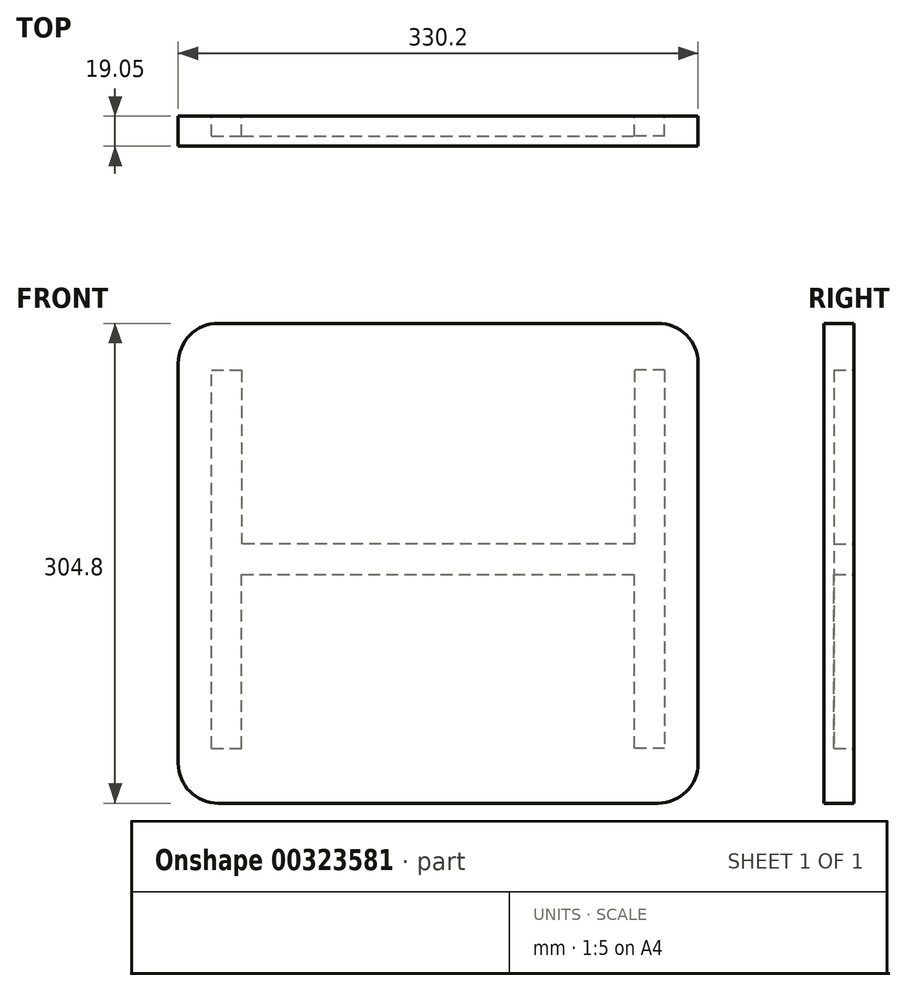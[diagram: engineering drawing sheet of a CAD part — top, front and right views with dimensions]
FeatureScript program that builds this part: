
annotation { "Feature Type Name" : "Feature", "Feature Type Description" : "" }
export const myFeature = defineFeature(function(context is Context, id is Id, definition is map)
    precondition{}
    {
        {
            var Q0;
            Q0=qCreatedBy(makeId("Front.planeOp"),FACE);
            var sketch = newSketch(context, id + "F0", { "sketchPlane" : qUnion([Q0])});
            skLineSegment(sketch, "E0", {"start": v(0, 163.43) * mm, "end": v(165.1, 163.43) * mm});
            skLineSegment(sketch, "E1.MirrorCS", {"start": v(0, 163.43) * mm, "end": v(-165.1, 163.43) * mm});
            skLineSegment(sketch, "E2", {"start": v(-165.1, 163.43) * mm, "end": v(-165.1, -141.37) * mm});
            skLineSegment(sketch, "E3", {"start": v(165.1, 163.43) * mm, "end": v(165.1, -141.37) * mm});
            skLineSegment(sketch, "E4", {"start": v(165.1, -141.37) * mm, "end": v(-165.1, -141.37) * mm});
            skSolve(sketch);
        }
        {
            var Q0;
            Q0 = qSketchRegion(id + "F0", true);
            extrude(context, id + "F1", {"entities" : qUnion([Q0]), "depth" : 19.05 * mm});
        }
        {
            var Q0;
            Q0=qCreatedBy(makeId("Front.planeOp"),FACE);
            var sketch = newSketch(context, id + "F2", { "sketchPlane" : qUnion([Q0])});
            skLineSegment(sketch, "E5", {"start": v(-166.8, 13.7) * mm, "end": v(0, 13.7) * mm, "construction": true});
            skLineSegment(sketch, "E6", {"start": v(0, -142.51) * mm, "end": v(0, 164.75) * mm, "construction": true});
            skLineSegment(sketch, "E7", {"start": v(0, 13.7) * mm, "end": v(165.2, 13.7) * mm, "construction": true});
            skLineSegment(sketch, "E8", {"start": v(143.88, 13.7) * mm, "end": v(143.88, 133.83) * mm});
            skLineSegment(sketch, "E9", {"start": v(143.88, 133.83) * mm, "end": v(124.83, 133.83) * mm});
            skLineSegment(sketch, "E10", {"start": v(124.83, 133.83) * mm, "end": v(124.83, 13.7) * mm});
            skLineSegment(sketch, "E11.MirrorCS", {"start": v(124.83, -106.45) * mm, "end": v(124.83, 13.7) * mm});
            skLineSegment(sketch, "E12.MirrorCS", {"start": v(143.88, 13.7) * mm, "end": v(143.88, -106.45) * mm});
            skLineSegment(sketch, "E13.MirrorCS", {"start": v(143.88, -106.45) * mm, "end": v(124.83, -106.45) * mm});
            skLineSegment(sketch, "E14.MirrorCS", {"start": v(-124.83, 133.83) * mm, "end": v(-124.83, 13.7) * mm});
            skLineSegment(sketch, "E15.MirrorCS", {"start": v(-143.88, 133.83) * mm, "end": v(-124.83, 133.83) * mm});
            skLineSegment(sketch, "E16.MirrorCS", {"start": v(-143.88, 13.7) * mm, "end": v(-143.88, 133.83) * mm});
            skLineSegment(sketch, "E17.MirrorCS", {"start": v(-143.88, 13.7) * mm, "end": v(-143.88, -106.45) * mm});
            skLineSegment(sketch, "E18.MirrorCS", {"start": v(-124.83, -106.45) * mm, "end": v(-124.83, 13.7) * mm});
            skLineSegment(sketch, "E19.MirrorCS", {"start": v(-143.88, -106.45) * mm, "end": v(-124.83, -106.45) * mm});
            skLineSegment(sketch, "E20", {"start": v(124.83, 133.83) * mm, "end": v(-124.83, 133.83) * mm, "construction": true});
            skLineSegment(sketch, "E21", {"start": v(110.9, 13.7) * mm, "end": v(110.9, 23.34) * mm, "construction": true});
            skLineSegment(sketch, "E22.MirrorCS", {"start": v(110.9, 13.7) * mm, "end": v(110.9, 4.04) * mm, "construction": true});
            skLineSegment(sketch, "E23", {"start": v(124.83, 23.34) * mm, "end": v(-124.83, 23.34) * mm});
            skLineSegment(sketch, "E24", {"start": v(-124.83, 23.34) * mm, "end": v(-124.83, 4.04) * mm});
            skLineSegment(sketch, "E25", {"start": v(-124.83, 4.04) * mm, "end": v(124.83, 4.04) * mm});
            skLineSegment(sketch, "E26", {"start": v(124.83, 4.04) * mm, "end": v(124.83, 23.34) * mm});
            skSolve(sketch);
        }
        {
            var Q0;
            Q0 = qSketchRegion(id + "F2", true);
            extrude(context, id + "F3", {"entities" : qUnion([Q0]), "operationType" : NewBodyOperationType.REMOVE, "depth" : 12.7 * mm});
        }
        {
            var Q0;
            Q0=makeQuery(id+"F1.opExtrude","SWEPT_EDGE",EDGE,{"disambiguationData":[OSD([sQuery(id+"F0.wireOp",EDGE,"E0"),sQuery(id+"F0.wireOp",EDGE,"E3")])]});
            fillet(context, id + "F4", {"entities" : qUnion([Q0]), "radius" : 25.4 * mm, "tangentPropagation" : true, "allowEdgeOverflow" : false});
        }
        {
            var Q0;
            Q0=makeQuery(id+"F1.opExtrude","SWEPT_EDGE",EDGE,{"disambiguationData":[OSD([sQuery(id+"F0.wireOp",EDGE,"E3"),sQuery(id+"F0.wireOp",EDGE,"E4")])]});
            fillet(context, id + "F5", {"entities" : qUnion([Q0]), "radius" : 25.4 * mm, "tangentPropagation" : true, "allowEdgeOverflow" : false});
        }
        {
            var Q0;
            Q0=makeQuery(id+"F1.opExtrude","SWEPT_EDGE",EDGE,{"disambiguationData":[OSD([sQuery(id+"F0.wireOp",EDGE,"E2"),sQuery(id+"F0.wireOp",EDGE,"E4")])]});
            fillet(context, id + "F6", {"entities" : qUnion([Q0]), "radius" : 25.4 * mm, "tangentPropagation" : true, "allowEdgeOverflow" : false});
        }
        {
            var Q0;
            Q0=makeQuery(id+"F1.opExtrude","SWEPT_EDGE",EDGE,{"disambiguationData":[OSD([sQuery(id+"F0.wireOp",EDGE,"E1.MirrorCS"),sQuery(id+"F0.wireOp",EDGE,"E2")])]});
            fillet(context, id + "F7", {"entities" : qUnion([Q0]), "radius" : 25.4 * mm, "tangentPropagation" : true, "allowEdgeOverflow" : false});
        }
    });
